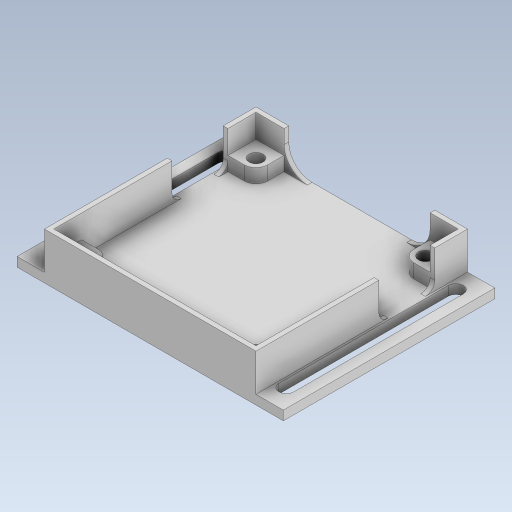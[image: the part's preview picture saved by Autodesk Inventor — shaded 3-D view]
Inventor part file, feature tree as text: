
AUTODESK INVENTOR PART (.ipt)
format: ipt  version: 2023.5 (Build 275446000, 446)  size: 483,328 bytes
history: native  units: mm
features: extrude x7, sketch x4
ambient origin geometry x8: Origin, YZ Plane, XZ Plane, XY Plane, X Axis, Y Axis, Z Axis, Center Point
bodies: Solid1 (feature_tree)
feature tree (11):
  sketch  "Sketch1"  dims[d0=43.3mm d1=43.3mm]
  extrude  "Extrusion1"  Depth=43.3mm
  extrude  "Extrusion2"  Depth=45.3mm
  extrude  "Extrusion3"  Depth=5.0mm
  extrude  "Extrusion4"  Depth=3.0mm
  extrude  "Extrusion5"  Depth=10.0mm TaperAngle=0.0deg
  extrude  "Extrusion6"  Depth=2.0mm TaperAngle=0.0deg
  extrude  "Extrusion7"  Depth=5.0mm TaperAngle=0.0deg
  sketch  "Sketch2"  dims[d2=45.3mm d3=45.3mm]
  sketch  "Sketch3"  dims[d4=5.0mm d5=3.5mm]
  sketch  "Sketch4"  dims[d6=3.5mm d7=3.0mm d8=10.0mm d9=0.0mm d10=2.0mm d11=0.0mm d12=5.0mm d13=0.0mm d14=3.0mm d15=57.0mm d16=3.2mm d17=2.0mm d18=2.0mm d19=0.0mm d20=45.3mm d21=2.0mm d22=0.0mm d23=5.0mm d24=2.0mm d25=2.0mm d26=0.0mm d27=12.0mm d28=2.0mm d29=2.0mm d30=0.0mm]
